# Revit family: Urinal_Contemporary_Lloyd_Elec-Valve-ADA_UE930_TOTO
name_source: partatom
category: Plumbing Fixtures
revit_build: Autodesk Revit Architecture 2013 (Build: 20130531_2115(x64)
units: mm (PartAtom-declared; Revit-internal decimal feet)

## types (1)
- UE930
    04 CSI = 22 42 13
    95 CSI = 15410
    ADA Compliant = Yes
    Assembly Code = D2010210
    Available in SanoGloss = No
    CAD Drawing URL = http://assets.totousa.com
    CW Connection = Yes
    CWFU = 0
    Certifications = IAPMO(cUPC), State of Massachusetts, City of Los Angeles
    Code Compliance = UPC, IPC, NSPC, NPC Canada, and others
    Cold Water Connection Diameter = 0' - 0 1/2"
    Cold Water Connection NPT Radius = 5/16"
    Cold Water Connection Radius = 0' - 0 1/4"
    Cold Water Connector = Cold Water Connection
    Color Availability = #01 Cotton
    Default Elevation = 2' - 0"
    Depth = 1' - 2"
    Description = Lloyd Urinal with Electronic Flush Valve - ADA
    Finish = Vitreous China - TOTO - 01 Cotton
    Flush Material = Vitreous China - TOTO - 01 Cotton
    Flush Valve Model = Flush Valve Model : TEY1DNC-42
    Gallons Per Flush = 1.0 gal
    HW Connection = No
    HWFU = 0
    Height = 2' - 5 1/4"
    Industry Standards = Meets and exceeds ASME A112.19.2/CSA B45.1
    Manufacturer = TOTO USA, Inc.
    Manufacturer Fax = (770) 282-0002
    Material = Vitreous China
    Model = UE930
    Mount Type = Wall
    Sanitary Connector = Waste Outlet Connection
    Series = Lloyd
    Shipping Weight = 57.30 lb
    Spec Sheet URL = http://assets.totousa.com
    Style = Contemporary
    Subcategory = Urinals
    Toto BIM Number = BM-00018
    URL = http://www.totousa.com
    Vent Connection = Yes
    WFU = 0
    Warranty = One Year Limited Warranty
    Warranty URL = http://www.totousa.com
    Waste Connection = Yes
    Waste Connection NPT Radius = 0' - 1"
    Width = 1' - 4 1/2"

## geometry (parser evidence)
native form markers: Blend x6, Sweep x5
no freeform markers — native parametric forms only
